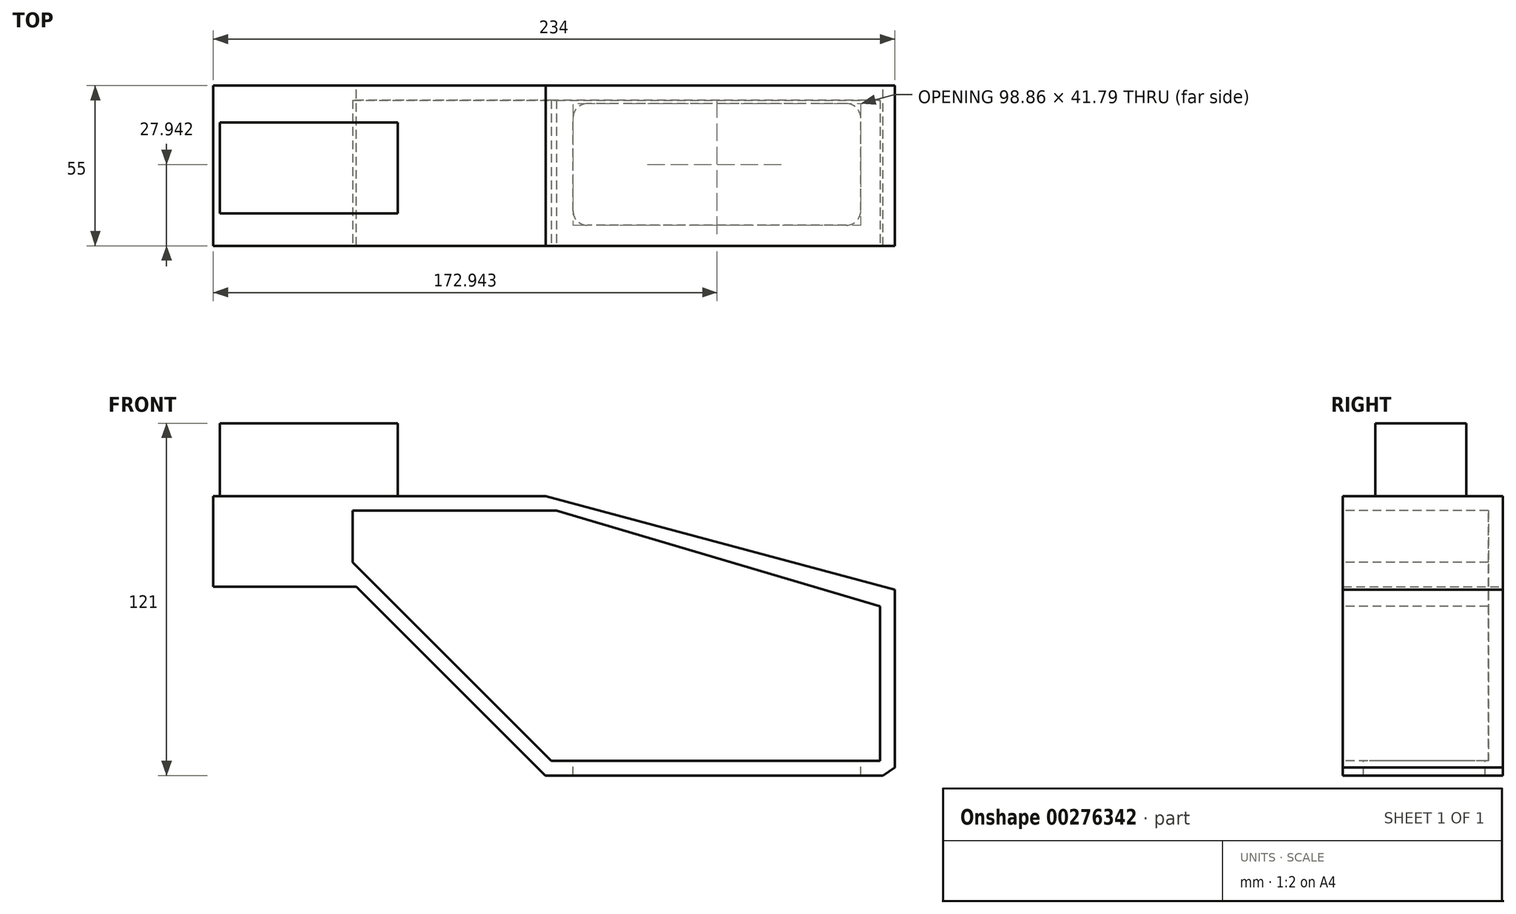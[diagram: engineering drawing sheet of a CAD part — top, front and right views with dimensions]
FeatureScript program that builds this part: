
annotation { "Feature Type Name" : "Feature", "Feature Type Description" : "" }
export const myFeature = defineFeature(function(context is Context, id is Id, definition is map)
    precondition{}
    {
        {
            var Q0;
            Q0=qCreatedBy(makeId("Front.planeOp"),FACE);
            var sketch = newSketch(context, id + "F0", { "sketchPlane" : qUnion([Q0])});
            skLineSegment(sketch, "E0.left", {"start": v(0, -52.09) * mm, "end": v(0, -113.12) * mm});
            skLineSegment(sketch, "E1", {"start": v(-4, -115.92) * mm, "end": v(0, -113.12) * mm});
            skLineSegment(sketch, "E2", {"start": v(-4, -115.92) * mm, "end": v(-120, -115.92) * mm});
            skLineSegment(sketch, "E3", {"start": v(-4, -115.92) * mm, "end": v(162.86, -115.92) * mm, "construction": true});
            skLineSegment(sketch, "E4", {"start": v(-184.9, -51.01) * mm, "end": v(-120, -115.92) * mm});
            skLineSegment(sketch, "E5", {"start": v(-234, -51.01) * mm, "end": v(-234, -19.92) * mm});
            skLineSegment(sketch, "E6", {"start": v(-184.9, -51.01) * mm, "end": v(-234, -51.01) * mm});
            skLineSegment(sketch, "E7", {"start": v(-119.83, -19.92) * mm, "end": v(0, -52.09) * mm});
            skLineSegment(sketch, "E8", {"start": v(-119.83, -19.92) * mm, "end": v(-234, -19.92) * mm});
            skSolve(sketch);
        }
        {
            var Q0;
            Q0 = qSketchRegion(id + "F0", true);
            extrude(context, id + "F1", {"entities" : qUnion([Q0]), "depth" : 55 * mm});
        }
        {
            var Q0;
            Q0=makeQuery(id+"F1.opExtrude","CAP_FACE",FACE,{"disambiguationData":[OSD([sQuery(id+"F0.wireOp",EDGE,"E0.bottom"),sQuery(id+"F0.wireOp",EDGE,"E0.left"),sQuery(id+"F0.wireOp",EDGE,"E1"),sQuery(id+"F0.wireOp",EDGE,"o98FWv03-F9f1-toG1-AfXk-xK1J4NO9c8Te"),sQuery(id+"F0.wireOp",EDGE,"E2"),sQuery(id+"F0.wireOp",EDGE,"E4"),sQuery(id+"F0.wireOp",EDGE,"E5")])],"isStart":false});
            var sketch = newSketch(context, id + "F2", { "sketchPlane" : qUnion([Q0])});
            skLineSegment(sketch, "E9", {"start": v(-186.2, -24.86) * mm, "end": v(-116.14, -24.86) * mm});
            skLineSegment(sketch, "E10", {"start": v(-5, -57.82) * mm, "end": v(-5, -110.92) * mm});
            skLineSegment(sketch, "E11", {"start": v(-5, -110.92) * mm, "end": v(-117.93, -110.92) * mm});
            skLineSegment(sketch, "E12", {"start": v(-117.93, -110.92) * mm, "end": v(-186.2, -42.65) * mm});
            skLineSegment(sketch, "E13", {"start": v(-186.2, -42.65) * mm, "end": v(-186.2, -24.86) * mm});
            skLineSegment(sketch, "E14", {"start": v(-116.14, -24.86) * mm, "end": v(-5, -57.82) * mm});
            skSolve(sketch);
        }
        {
            var Q0;
            Q0 = qSketchRegion(id + "F2", true);
            var Q1;
            Q1=makeQuery(id+"F1.opExtrude","CAP_FACE",FACE,{"disambiguationData":[OSD([sQuery(id+"F0.wireOp",EDGE,"E0.bottom"),sQuery(id+"F0.wireOp",EDGE,"E0.left"),sQuery(id+"F0.wireOp",EDGE,"E1"),sQuery(id+"F0.wireOp",EDGE,"o98FWv03-F9f1-toG1-AfXk-xK1J4NO9c8Te"),sQuery(id+"F0.wireOp",EDGE,"E2"),sQuery(id+"F0.wireOp",EDGE,"E4"),sQuery(id+"F0.wireOp",EDGE,"E5")])],"isStart":true});
            extrude(context, id + "F3", {"entities" : qUnion([Q0]), "operationType" : NewBodyOperationType.REMOVE, "oppositeDirection" : true, "endBoundEntityFace" : qUnion([Q1]), "depth" : 50 * mm, "hasSecondDirection" : true, "secondDirectionOppositeDirection" : false, "secondDirectionDepth" : 50 * mm});
        }
        {
            var Q0;
            Q0=makeQuery(id+"F3.boolean.opBoolean","COPY",FACE,{"derivedFrom":makeQuery(id+"F3.opExtrude","SWEPT_FACE",FACE,{"disambiguationData":[OSD([sQuery(id+"F2.wireOp",EDGE,"E11")])]})});
            var sketch = newSketch(context, id + "F4", { "sketchPlane" : qUnion([Q0])});
            skLineSegment(sketch, "E15.bottom", {"start": v(-105.49, -6.16) * mm, "end": v(-16.63, -6.16) * mm});
            skLineSegment(sketch, "E15.top", {"start": v(-105.49, -47.95) * mm, "end": v(-16.63, -47.95) * mm});
            skLineSegment(sketch, "E15.left", {"start": v(-110.49, -11.16) * mm, "end": v(-110.49, -42.95) * mm});
            skLineSegment(sketch, "E15.right", {"start": v(-11.63, -11.16) * mm, "end": v(-11.63, -42.95) * mm});
            skPoint(sketch, "E16.visualSharp", {"position": v(-110.49, -47.95) * mm});
            skArc(sketch, "E16.filletArc", {"start": v(-110.49, -42.95) * mm, "mid": v(-109.02, -46.49) * mm, "end": v(-105.49, -47.95) * mm});
            skPoint(sketch, "E17.visualSharp", {"position": v(-11.63, -47.95) * mm});
            skArc(sketch, "E17.filletArc", {"start": v(-16.63, -47.95) * mm, "mid": v(-13.1, -46.49) * mm, "end": v(-11.63, -42.95) * mm});
            skPoint(sketch, "E18.visualSharp", {"position": v(-11.63, -6.16) * mm});
            skArc(sketch, "E18.filletArc", {"start": v(-11.63, -11.16) * mm, "mid": v(-13.1, -7.63) * mm, "end": v(-16.63, -6.16) * mm});
            skPoint(sketch, "E19.visualSharp", {"position": v(-110.49, -6.16) * mm});
            skArc(sketch, "E19.filletArc", {"start": v(-105.49, -6.16) * mm, "mid": v(-109.02, -7.63) * mm, "end": v(-110.49, -11.16) * mm});
            skSolve(sketch);
        }
        {
            var Q0;
            Q0 = qSketchRegion(id + "F4", true);
            extrude(context, id + "F5", {"entities" : qUnion([Q0]), "operationType" : NewBodyOperationType.REMOVE, "oppositeDirection" : true, "depth" : 25 * mm});
        }
        {
            var Q0;
            Q0=makeQuery(id+"F1.opExtrude","SWEPT_FACE",FACE,{"disambiguationData":[OSD([sQuery(id+"F0.wireOp",EDGE,"E8")])]});
            cPlane(context, id + "F6", {"entities" : qUnion([Q0]), "cplaneType" : CPlaneType.OFFSET, "offset" : 0 * mm, "width" : 150 * mm, "height" : 150 * mm});
        }
        {
            var Q0;
            Q0=qCreatedBy(id+"F6.planeOp",FACE);
            var sketch = newSketch(context, id + "F7", { "sketchPlane" : qUnion([Q0])});
            skLineSegment(sketch, "E20.bottom", {"start": v(-231.75, -12.62) * mm, "end": v(-170.66, -12.62) * mm});
            skLineSegment(sketch, "E20.top", {"start": v(-231.75, -43.93) * mm, "end": v(-170.66, -43.93) * mm});
            skLineSegment(sketch, "E20.left", {"start": v(-231.75, -12.62) * mm, "end": v(-231.75, -43.93) * mm});
            skLineSegment(sketch, "E20.right", {"start": v(-170.66, -12.62) * mm, "end": v(-170.66, -43.93) * mm});
            skSolve(sketch);
        }
        {
            var Q0;
            Q0=makeQuery(id+"F7.imprint","IMPRINT",FACE,{"disambiguationData":[TD([[makeQuery(id+"F7.imprint","IMPRINT",EDGE,{"derivedFrom":sQuery(id+"F7.wireOp",EDGE,"E20.bottom")}),-1.0]])]});
            extrude(context, id + "F8", {"entities" : qUnion([Q0]), "depth" : 25 * mm});
        }
    });
